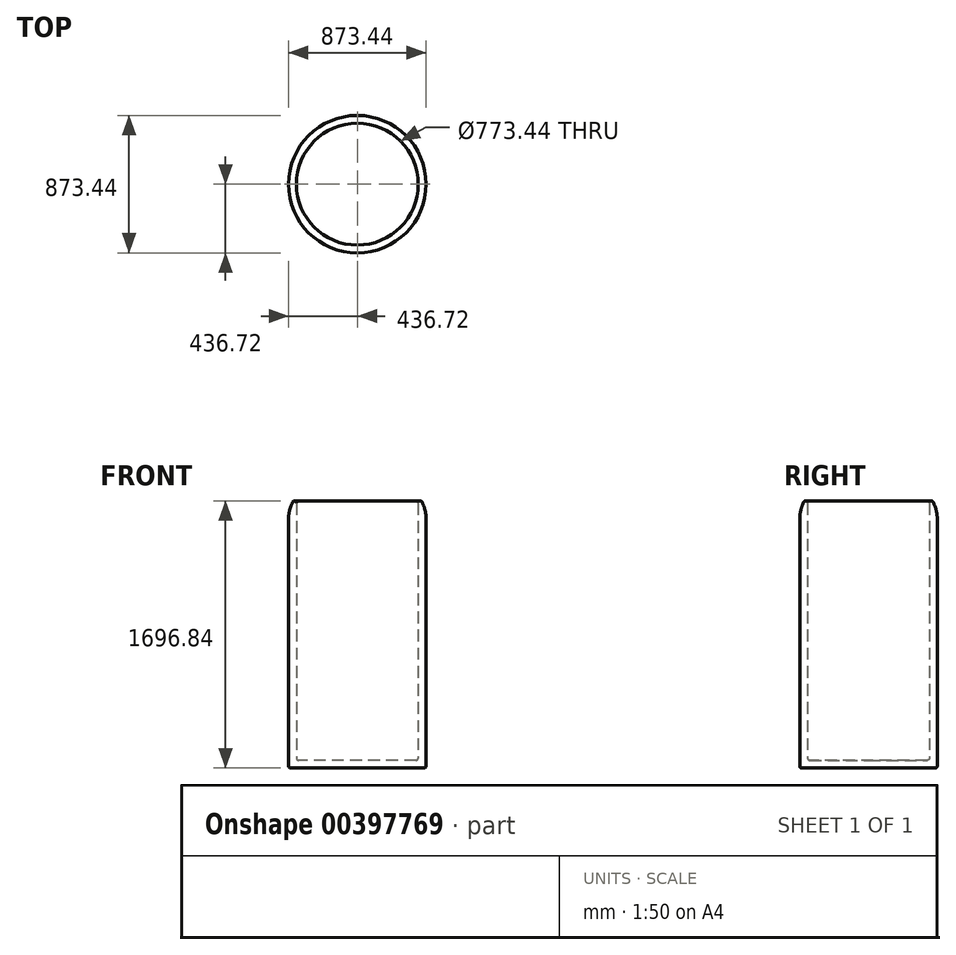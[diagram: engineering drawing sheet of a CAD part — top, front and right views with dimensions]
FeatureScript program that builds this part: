
annotation { "Feature Type Name" : "Feature", "Feature Type Description" : "" }
export const myFeature = defineFeature(function(context is Context, id is Id, definition is map)
    precondition{}
    {
        {
            var Q0;
            Q0=qCreatedBy(makeId("Top.planeOp"),FACE);
            var sketch = newSketch(context, id + "F0", { "sketchPlane" : qUnion([Q0])});
            skCircle(sketch, "E0", {"center": v(0, 0) * mm, "radius": 436.72 * mm});
            skSolve(sketch);
        }
        {
            var Q0;
            Q0 = qSketchRegion(id + "F0", true);
            extrude(context, id + "F1", {"entities" : qUnion([Q0]), "depth" : 1727.2 * mm});
        }
        {
            var Q0;
            Q0=makeQuery(id+"F1.opExtrude","CAP_FACE",FACE,{"disambiguationData":[OSD([sQuery(id+"F0.wireOp",EDGE,"E0")])],"isStart":false});
            shell(context, id + "F2", {"entities" : qUnion([Q0]), "thickness" : 50 * mm});
        }
        {
            var Q0;
            Q0=makeQuery(id+"F1.opExtrude","CAP_EDGE",EDGE,{"disambiguationData":[OSD([sQuery(id+"F0.wireOp",EDGE,"E0")])],"isStart":false});
            fillet(context, id + "F3", {"entities" : qUnion([Q0]), "radius" : 233.02 * mm, "tangentPropagation" : true, "allowEdgeOverflow" : false});
        }
        {
            var Q0;
            Q0=makeQuery(id+"F1.opExtrude","CAP_EDGE",EDGE,{"disambiguationData":[OSD([sQuery(id+"F0.wireOp",EDGE,"E0")])],"isStart":true});
            var Q1;
            {var subQ0=sQuery(id+"F0.wireOp",EDGE,"E0");Q1=makeQuery(id+"F2.opShell","OFFSET_FACE",FACE,{"disambiguationData":[OSD([subQ0]),TDD([makeQuery(id+"F1.opExtrude","SWEPT_FACE",FACE,{"disambiguationData":[OSD([subQ0])]})])]});}
            fillet(context, id + "F4", {"entities" : qUnion([Q0, Q1]), "radius" : 12.7 * mm, "tangentPropagation" : true, "allowEdgeOverflow" : false});
        }
    });
